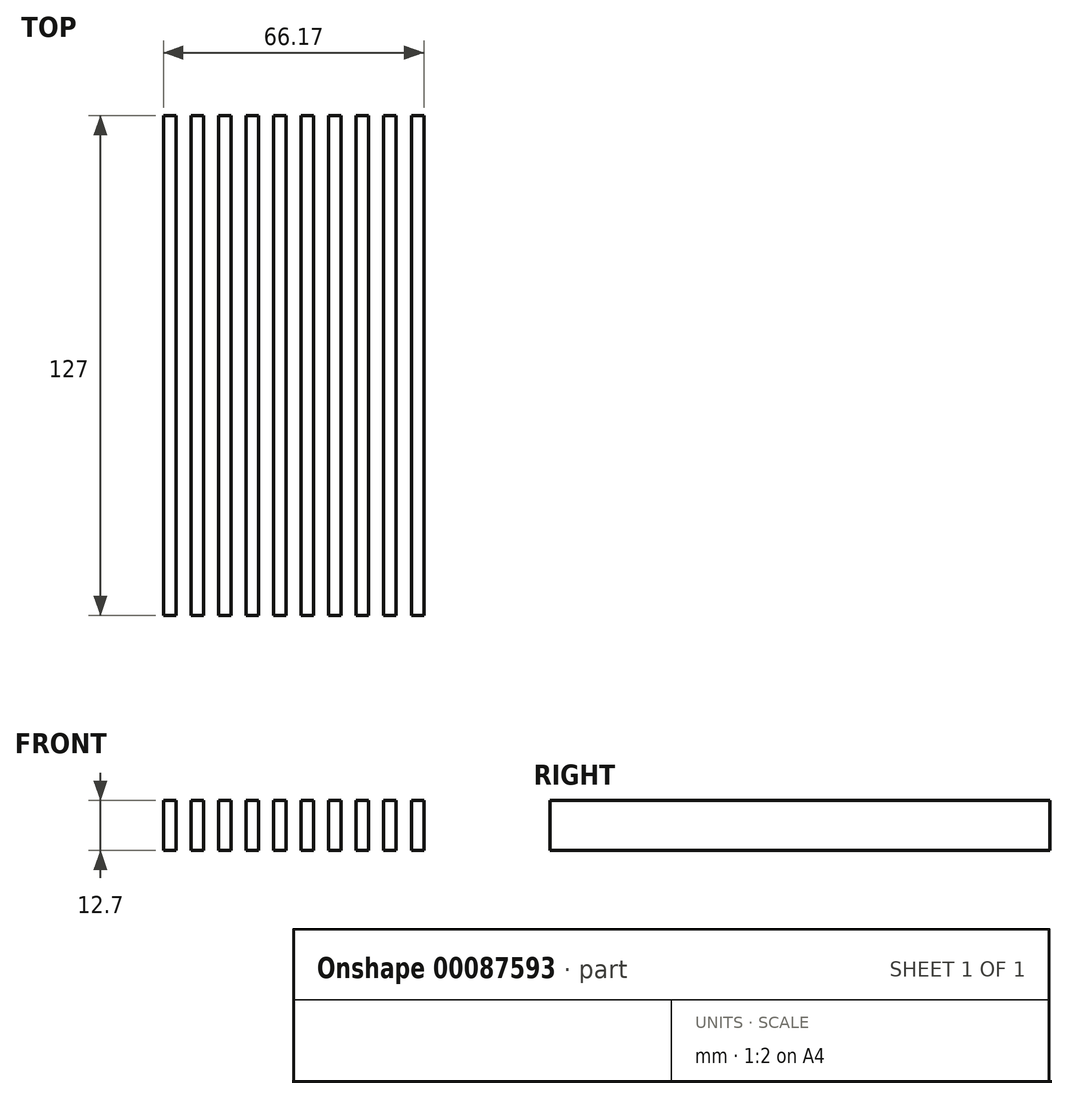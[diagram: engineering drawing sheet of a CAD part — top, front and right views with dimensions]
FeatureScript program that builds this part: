
annotation { "Feature Type Name" : "Feature", "Feature Type Description" : "" }
export const myFeature = defineFeature(function(context is Context, id is Id, definition is map)
    precondition{}
    {
        {
            var Q0;
            Q0=qCreatedBy(makeId("Front.planeOp"),FACE);
            var sketch = newSketch(context, id + "F0", { "sketchPlane" : qUnion([Q0])});
            skLineSegment(sketch, "E0.bottom", {"start": v(0, 0) * mm, "end": v(3.18, 0) * mm});
            skLineSegment(sketch, "E0.top", {"start": v(0, 12.7) * mm, "end": v(3.17, 12.7) * mm});
            skLineSegment(sketch, "E0.left", {"start": v(0, 0) * mm, "end": v(0, 12.7) * mm});
            skLineSegment(sketch, "E0.right", {"start": v(3.18, 0) * mm, "end": v(3.18, 12.7) * mm});
            skLineSegment(sketch, "E1.1.0.0", {"start": v(7, 12.7) * mm, "end": v(10.17, 12.7) * mm});
            skLineSegment(sketch, "E1.1.0.1", {"start": v(7, 0) * mm, "end": v(7, 12.7) * mm});
            skLineSegment(sketch, "E1.1.0.2", {"start": v(10.18, 0) * mm, "end": v(10.18, 12.7) * mm});
            skLineSegment(sketch, "E1.1.0.3", {"start": v(7, 0) * mm, "end": v(10.18, 0) * mm});
            skLineSegment(sketch, "E1.2.0.0", {"start": v(14, 12.7) * mm, "end": v(17.17, 12.7) * mm});
            skLineSegment(sketch, "E1.2.0.1", {"start": v(14, 0) * mm, "end": v(14, 12.7) * mm});
            skLineSegment(sketch, "E1.2.0.2", {"start": v(17.18, 0) * mm, "end": v(17.18, 12.7) * mm});
            skLineSegment(sketch, "E1.2.0.3", {"start": v(14, 0) * mm, "end": v(17.18, 0) * mm});
            skLineSegment(sketch, "E1.3.0.0", {"start": v(21, 12.7) * mm, "end": v(24.17, 12.7) * mm});
            skLineSegment(sketch, "E1.3.0.1", {"start": v(21, 0) * mm, "end": v(21, 12.7) * mm});
            skLineSegment(sketch, "E1.3.0.2", {"start": v(24.18, 0) * mm, "end": v(24.18, 12.7) * mm});
            skLineSegment(sketch, "E1.3.0.3", {"start": v(21, 0) * mm, "end": v(24.17, 0) * mm});
            skLineSegment(sketch, "E1.4.0.0", {"start": v(28, 12.7) * mm, "end": v(31.17, 12.7) * mm});
            skLineSegment(sketch, "E1.4.0.1", {"start": v(28, 0) * mm, "end": v(28, 12.7) * mm});
            skLineSegment(sketch, "E1.4.0.2", {"start": v(31.18, 0) * mm, "end": v(31.18, 12.7) * mm});
            skLineSegment(sketch, "E1.4.0.3", {"start": v(28, 0) * mm, "end": v(31.17, 0) * mm});
            skLineSegment(sketch, "E1.5.0.0", {"start": v(35, 12.7) * mm, "end": v(38.17, 12.7) * mm});
            skLineSegment(sketch, "E1.5.0.1", {"start": v(35, 0) * mm, "end": v(35, 12.7) * mm});
            skLineSegment(sketch, "E1.5.0.2", {"start": v(38.17, 0) * mm, "end": v(38.17, 12.7) * mm});
            skLineSegment(sketch, "E1.5.0.3", {"start": v(35, 0) * mm, "end": v(38.17, 0) * mm});
            skLineSegment(sketch, "E1.6.0.0", {"start": v(42, 12.7) * mm, "end": v(45.17, 12.7) * mm});
            skLineSegment(sketch, "E1.6.0.1", {"start": v(42, 0) * mm, "end": v(42, 12.7) * mm});
            skLineSegment(sketch, "E1.6.0.2", {"start": v(45.17, 0) * mm, "end": v(45.17, 12.7) * mm});
            skLineSegment(sketch, "E1.6.0.3", {"start": v(42, 0) * mm, "end": v(45.17, 0) * mm});
            skLineSegment(sketch, "E1.7.0.0", {"start": v(49, 12.7) * mm, "end": v(52.17, 12.7) * mm});
            skLineSegment(sketch, "E1.7.0.1", {"start": v(49, 0) * mm, "end": v(49, 12.7) * mm});
            skLineSegment(sketch, "E1.7.0.2", {"start": v(52.17, 0) * mm, "end": v(52.17, 12.7) * mm});
            skLineSegment(sketch, "E1.7.0.3", {"start": v(49, 0) * mm, "end": v(52.17, 0) * mm});
            skLineSegment(sketch, "E1.8.0.0", {"start": v(56, 12.7) * mm, "end": v(59.17, 12.7) * mm});
            skLineSegment(sketch, "E1.8.0.1", {"start": v(56, 0) * mm, "end": v(56, 12.7) * mm});
            skLineSegment(sketch, "E1.8.0.2", {"start": v(59.17, 0) * mm, "end": v(59.17, 12.7) * mm});
            skLineSegment(sketch, "E1.8.0.3", {"start": v(56, 0) * mm, "end": v(59.17, 0) * mm});
            skLineSegment(sketch, "E1.9.0.0", {"start": v(63, 12.7) * mm, "end": v(66.17, 12.7) * mm});
            skLineSegment(sketch, "E1.9.0.1", {"start": v(63, 0) * mm, "end": v(63, 12.7) * mm});
            skLineSegment(sketch, "E1.9.0.2", {"start": v(66.17, 0) * mm, "end": v(66.17, 12.7) * mm});
            skLineSegment(sketch, "E1.9.0.3", {"start": v(63, 0) * mm, "end": v(66.18, 0) * mm});
            skLineSegment(sketch, "E1.direction1", {"start": v(0, 0) * mm, "end": v(7, 0) * mm, "construction": true});
            skSolve(sketch);
        }
        {
            var Q0;
            Q0 = qSketchRegion(id + "F0", true);
            extrude(context, id + "F1", {"entities" : qUnion([Q0]), "depth" : 127 * mm});
        }
    });
